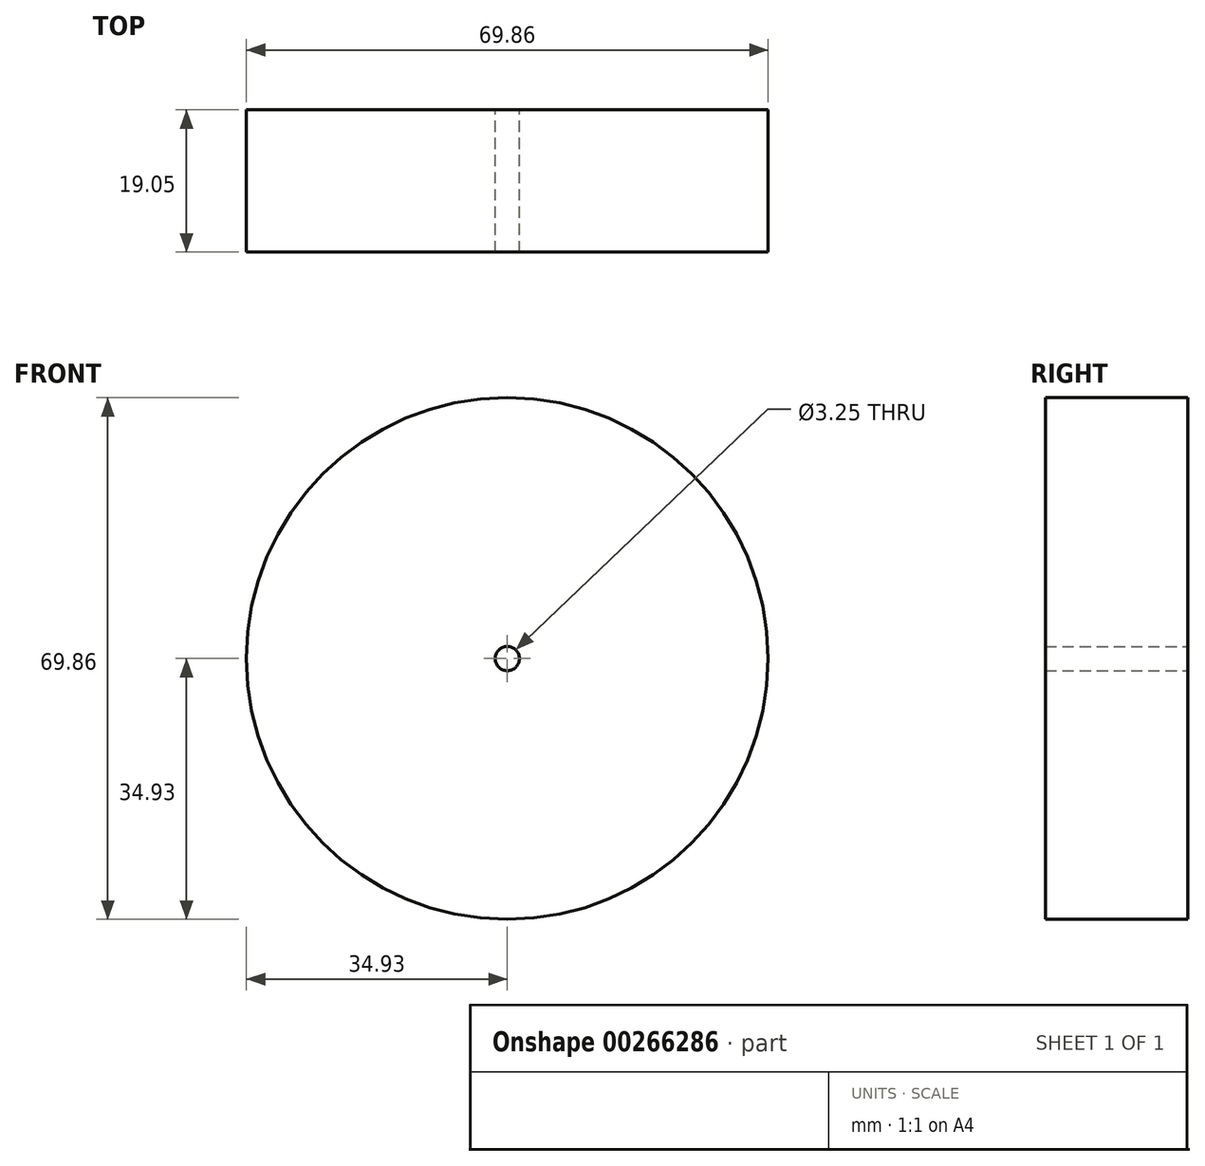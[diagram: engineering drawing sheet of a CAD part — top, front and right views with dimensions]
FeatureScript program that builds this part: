
annotation { "Feature Type Name" : "Feature", "Feature Type Description" : "" }
export const myFeature = defineFeature(function(context is Context, id is Id, definition is map)
    precondition{}
    {
        {
            var Q0;
            Q0=qCreatedBy(makeId("Front.planeOp"),FACE);
            var sketch = newSketch(context, id + "F0", { "sketchPlane" : qUnion([Q0])});
            skCircle(sketch, "E0", {"center": v(0, 0) * mm, "radius": 34.93 * mm});
            skCircle(sketch, "E1", {"center": v(0, 0) * mm, "radius": 1.63 * mm});
            skSolve(sketch);
        }
        {
            var Q0;
            Q0=makeQuery(id+"F0.imprint","IMPRINT",FACE,{"disambiguationData":[TD([[makeQuery(id+"F0.imprint","IMPRINT",EDGE,{"derivedFrom":sQuery(id+"F0.wireOp",EDGE,"E0")}),1.0]])]});
            extrude(context, id + "F1", {"entities" : qUnion([Q0]), "depth" : 19.05 * mm});
        }
    });
